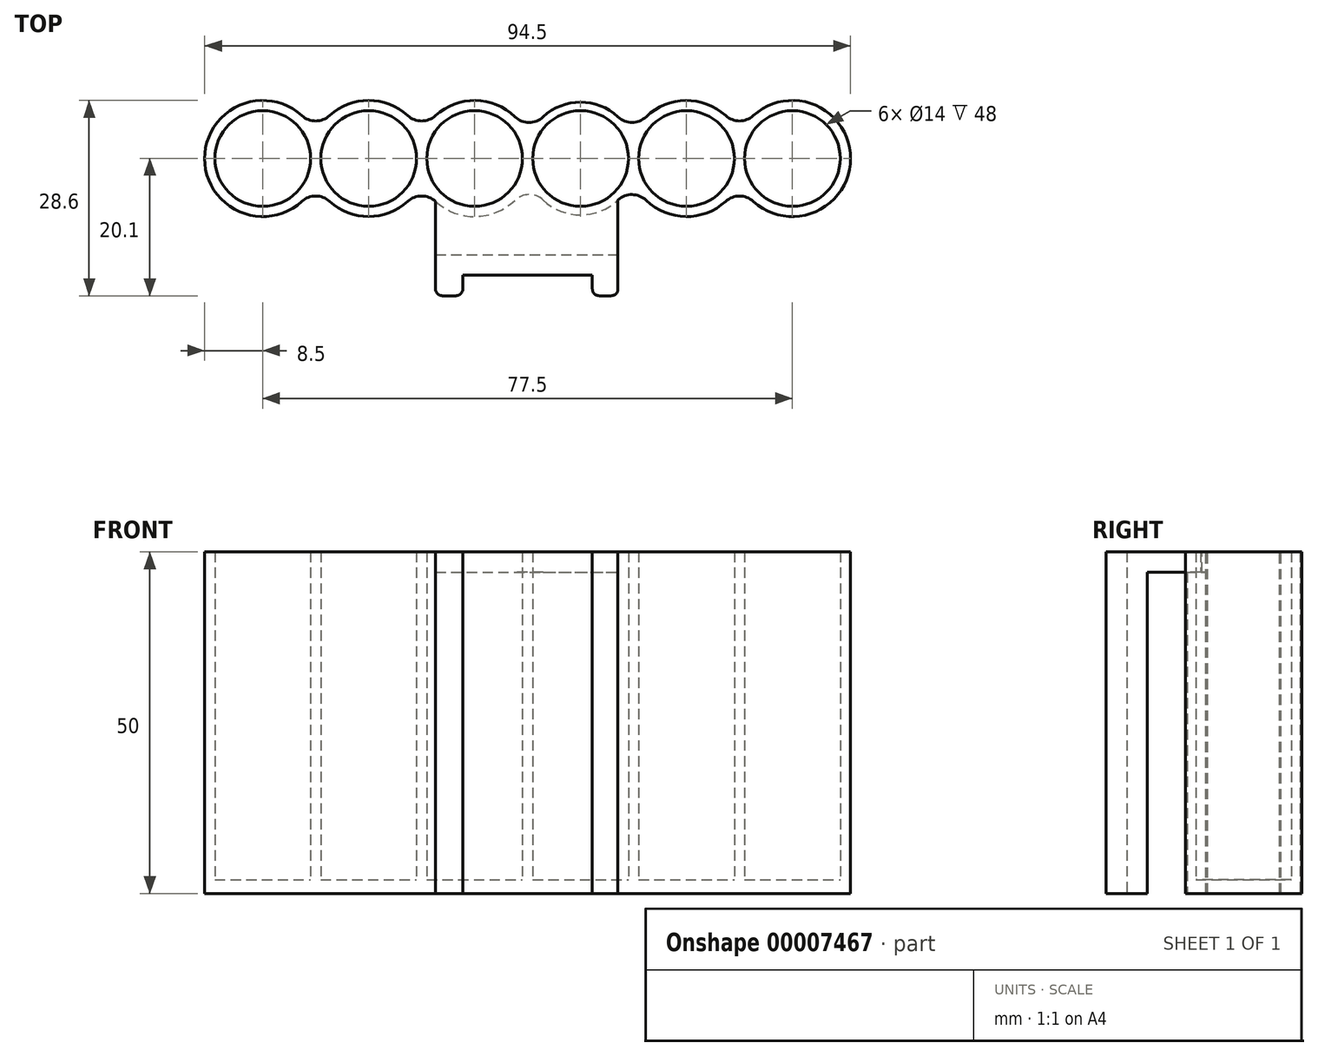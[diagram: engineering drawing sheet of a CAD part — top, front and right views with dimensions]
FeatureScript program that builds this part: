
annotation { "Feature Type Name" : "Feature", "Feature Type Description" : "" }
export const myFeature = defineFeature(function(context is Context, id is Id, definition is map)
    precondition{}
    {
        {
            var Q0;
            Q0=qCreatedBy(makeId("Top.planeOp"),FACE);
            var sketch = newSketch(context, id + "F0", { "sketchPlane" : qUnion([Q0])});
            skCircle(sketch, "E0", {"center": v(7.75, 0) * mm, "radius": 7 * mm});
            skCircle(sketch, "E1", {"center": v(23.25, 0) * mm, "radius": 7 * mm});
            skCircle(sketch, "E2", {"center": v(38.75, 0) * mm, "radius": 7 * mm});
            skCircle(sketch, "E3.0.MirrorC", {"center": v(-7.75, 0) * mm, "radius": 7 * mm});
            skCircle(sketch, "E4.0.MirrorC", {"center": v(-23.25, 0) * mm, "radius": 7 * mm});
            skCircle(sketch, "E5.0.MirrorC", {"center": v(-38.75, 0) * mm, "radius": 7 * mm});
            skArc(sketch, "E6", {"start": v(-31, 3.5) * mm, "mid": v(-47.25, 0) * mm, "end": v(-31, -3.5) * mm});
            skArc(sketch, "E7", {"start": v(-31, -3.5) * mm, "mid": v(-23.25, -8.5) * mm, "end": v(-15.5, -3.5) * mm});
            skArc(sketch, "E8", {"start": v(-15.5, -3.5) * mm, "mid": v(-7.46, -8.5) * mm, "end": v(0.22, -2.96) * mm});
            skArc(sketch, "E9", {"start": v(15.28, -2.96) * mm, "mid": v(22.96, -8.5) * mm, "end": v(31, -3.5) * mm});
            skArc(sketch, "E10", {"start": v(31, -3.5) * mm, "mid": v(47.25, 0) * mm, "end": v(31, 3.5) * mm});
            skArc(sketch, "E11.trimOffspring", {"start": v(-15.5, 3.5) * mm, "mid": v(-23.25, 8.5) * mm, "end": v(-31, 3.5) * mm});
            skArc(sketch, "E12.trimOffspring", {"start": v(0.22, 2.96) * mm, "mid": v(-7.46, 8.5) * mm, "end": v(-15.5, 3.5) * mm});
            skArc(sketch, "E13.trimOffspring", {"start": v(15.28, 2.96) * mm, "mid": v(7.75, 8.26) * mm, "end": v(0.22, 2.96) * mm});
            skArc(sketch, "E14.trimOffspring", {"start": v(31, 3.5) * mm, "mid": v(22.96, 8.5) * mm, "end": v(15.28, 2.96) * mm});
            skArc(sketch, "E15.trimOffspring", {"start": v(0.22, -2.96) * mm, "mid": v(7.75, -8.26) * mm, "end": v(15.28, -2.96) * mm});
            skSolve(sketch);
        }
        {
            var Q0;
            Q0 = qSketchRegion(id + "F0", true);
            extrude(context, id + "F1", {"entities" : qUnion([Q0]), "depth" : 50 * mm});
        }
        {
            var Q0;
            Q0=makeQuery(id+"F1.opExtrude","SWEPT_EDGE",EDGE,{"disambiguationData":[OSD([sQuery(id+"F0.wireOp",EDGE,"E6"),sQuery(id+"F0.wireOp",EDGE,"E11.trimOffspring")])]});
            var Q1;
            Q1=makeQuery(id+"F1.opExtrude","SWEPT_EDGE",EDGE,{"disambiguationData":[OSD([sQuery(id+"F0.wireOp",EDGE,"E11.trimOffspring"),sQuery(id+"F0.wireOp",EDGE,"E12.trimOffspring")])]});
            var Q2;
            Q2=makeQuery(id+"F1.opExtrude","SWEPT_EDGE",EDGE,{"disambiguationData":[OSD([sQuery(id+"F0.wireOp",EDGE,"E12.trimOffspring"),sQuery(id+"F0.wireOp",EDGE,"E13.trimOffspring")])]});
            var Q3;
            Q3=makeQuery(id+"F1.opExtrude","SWEPT_EDGE",EDGE,{"disambiguationData":[OSD([sQuery(id+"F0.wireOp",EDGE,"E13.trimOffspring"),sQuery(id+"F0.wireOp",EDGE,"E14.trimOffspring")])]});
            var Q4;
            Q4=makeQuery(id+"F1.opExtrude","SWEPT_EDGE",EDGE,{"disambiguationData":[OSD([sQuery(id+"F0.wireOp",EDGE,"E10"),sQuery(id+"F0.wireOp",EDGE,"E14.trimOffspring")])]});
            var Q5;
            Q5=makeQuery(id+"F1.opExtrude","SWEPT_EDGE",EDGE,{"disambiguationData":[OSD([sQuery(id+"F0.wireOp",EDGE,"E6"),sQuery(id+"F0.wireOp",EDGE,"E7")])]});
            var Q6;
            Q6=makeQuery(id+"F1.opExtrude","SWEPT_EDGE",EDGE,{"disambiguationData":[OSD([sQuery(id+"F0.wireOp",EDGE,"E7"),sQuery(id+"F0.wireOp",EDGE,"E8")])]});
            var Q7;
            Q7=makeQuery(id+"F1.opExtrude","SWEPT_EDGE",EDGE,{"disambiguationData":[OSD([sQuery(id+"F0.wireOp",EDGE,"E8"),sQuery(id+"F0.wireOp",EDGE,"1430ee90-bdf1-449c-a1c4-02042bd7a36f")])]});
            var Q8;
            Q8=makeQuery(id+"F1.opExtrude","SWEPT_EDGE",EDGE,{"disambiguationData":[OSD([sQuery(id+"F0.wireOp",EDGE,"1430ee90-bdf1-449c-a1c4-02042bd7a36f"),sQuery(id+"F0.wireOp",EDGE,"E9")])]});
            var Q9;
            Q9=makeQuery(id+"F1.opExtrude","SWEPT_EDGE",EDGE,{"disambiguationData":[OSD([sQuery(id+"F0.wireOp",EDGE,"E9"),sQuery(id+"F0.wireOp",EDGE,"E10")])]});
            fillet(context, id + "F2", {"entities" : qUnion([Q0, Q1, Q2, Q3, Q4, Q5, Q6, Q7, Q8, Q9]), "radius" : 3 * mm, "tangentPropagation" : true, "allowEdgeOverflow" : false});
        }
        {
            var Q0;
            Q0=makeQuery(id+"F1.opExtrude","CAP_FACE",FACE,{"disambiguationData":[OSD([sQuery(id+"F0.wireOp",EDGE,"E0"),sQuery(id+"F0.wireOp",EDGE,"E1"),sQuery(id+"F0.wireOp",EDGE,"E2"),sQuery(id+"F0.wireOp",EDGE,"E3.0.MirrorC"),sQuery(id+"F0.wireOp",EDGE,"E4.0.MirrorC"),sQuery(id+"F0.wireOp",EDGE,"E5.0.MirrorC"),sQuery(id+"F0.wireOp",EDGE,"E6"),sQuery(id+"F0.wireOp",EDGE,"E7"),sQuery(id+"F0.wireOp",EDGE,"E8"),sQuery(id+"F0.wireOp",EDGE,"1430ee90-bdf1-449c-a1c4-02042bd7a36f"),sQuery(id+"F0.wireOp",EDGE,"E9"),sQuery(id+"F0.wireOp",EDGE,"E10"),sQuery(id+"F0.wireOp",EDGE,"E11.trimOffspring"),sQuery(id+"F0.wireOp",EDGE,"E12.trimOffspring"),sQuery(id+"F0.wireOp",EDGE,"E13.trimOffspring"),sQuery(id+"F0.wireOp",EDGE,"E14.trimOffspring")])],"isStart":true});
            var sketch = newSketch(context, id + "F3", { "sketchPlane" : qUnion([Q0])});
            skArc(sketch, "E16.0", {"start": v(33.02, 6.28) * mm, "mid": v(47.25, 0) * mm, "end": v(33.02, -6.28) * mm});
            skArc(sketch, "E17.0", {"start": v(28.98, 6.28) * mm, "mid": v(31, 5.5) * mm, "end": v(33.02, 6.28) * mm});
            skArc(sketch, "E18.0", {"start": v(17.35, 6.12) * mm, "mid": v(23.14, 8.5) * mm, "end": v(28.98, 6.28) * mm});
            skArc(sketch, "E19.0", {"start": v(13.22, 6.1) * mm, "mid": v(15.3, 5.28) * mm, "end": v(17.35, 6.12) * mm});
            skArc(sketch, "E20.0", {"start": v(2.28, 6.1) * mm, "mid": v(7.75, 8.26) * mm, "end": v(13.22, 6.1) * mm});
            skArc(sketch, "E21.0", {"start": v(-1.85, 6.12) * mm, "mid": v(0.2, 5.28) * mm, "end": v(2.28, 6.1) * mm});
            skArc(sketch, "E22.0", {"start": v(-13.48, 6.28) * mm, "mid": v(-7.64, 8.5) * mm, "end": v(-1.85, 6.12) * mm});
            skArc(sketch, "E23.0", {"start": v(-17.52, 6.28) * mm, "mid": v(-15.5, 5.5) * mm, "end": v(-13.48, 6.28) * mm});
            skArc(sketch, "E24.0", {"start": v(-28.98, 6.28) * mm, "mid": v(-23.25, 8.5) * mm, "end": v(-17.52, 6.28) * mm});
            skArc(sketch, "E25.0", {"start": v(-33.02, 6.28) * mm, "mid": v(-31, 5.5) * mm, "end": v(-28.98, 6.28) * mm});
            skArc(sketch, "E26.0", {"start": v(-33.02, -6.28) * mm, "mid": v(-47.25, 0) * mm, "end": v(-33.02, 6.28) * mm});
            skArc(sketch, "E27.0", {"start": v(-28.98, -6.28) * mm, "mid": v(-31, -5.5) * mm, "end": v(-33.02, -6.28) * mm});
            skArc(sketch, "E28.0", {"start": v(-17.52, -6.28) * mm, "mid": v(-23.25, -8.5) * mm, "end": v(-28.98, -6.28) * mm});
            skArc(sketch, "E29.0", {"start": v(-13.48, -6.28) * mm, "mid": v(-15.5, -5.5) * mm, "end": v(-17.52, -6.28) * mm});
            skArc(sketch, "E30.0", {"start": v(-1.85, -6.12) * mm, "mid": v(-7.64, -8.5) * mm, "end": v(-13.48, -6.28) * mm});
            skArc(sketch, "E31.0", {"start": v(2.28, -6.1) * mm, "mid": v(0.2, -5.28) * mm, "end": v(-1.85, -6.12) * mm});
            skArc(sketch, "E32.0", {"start": v(13.22, -6.1) * mm, "mid": v(7.75, -8.26) * mm, "end": v(2.28, -6.1) * mm});
            skArc(sketch, "E33.0", {"start": v(17.35, -6.12) * mm, "mid": v(15.3, -5.28) * mm, "end": v(13.22, -6.1) * mm});
            skArc(sketch, "E34.0", {"start": v(28.98, -6.28) * mm, "mid": v(23.14, -8.5) * mm, "end": v(17.35, -6.12) * mm});
            skArc(sketch, "E35.0", {"start": v(33.02, -6.28) * mm, "mid": v(31, -5.5) * mm, "end": v(28.98, -6.28) * mm});
            skSolve(sketch);
        }
        {
            var Q0;
            Q0 = qSketchRegion(id + "F3", true);
            extrude(context, id + "F4", {"entities" : qUnion([Q0]), "operationType" : NewBodyOperationType.ADD, "oppositeDirection" : true, "depth" : 2 * mm});
        }
        {
            var Q0;
            Q0=makeQuery(id+"F1.opExtrude","CAP_FACE",FACE,{"disambiguationData":[OSD([sQuery(id+"F0.wireOp",EDGE,"E0"),sQuery(id+"F0.wireOp",EDGE,"E1"),sQuery(id+"F0.wireOp",EDGE,"E2"),sQuery(id+"F0.wireOp",EDGE,"E3.0.MirrorC"),sQuery(id+"F0.wireOp",EDGE,"E4.0.MirrorC"),sQuery(id+"F0.wireOp",EDGE,"E5.0.MirrorC"),sQuery(id+"F0.wireOp",EDGE,"E6"),sQuery(id+"F0.wireOp",EDGE,"E7"),sQuery(id+"F0.wireOp",EDGE,"E8"),sQuery(id+"F0.wireOp",EDGE,"1430ee90-bdf1-449c-a1c4-02042bd7a36f"),sQuery(id+"F0.wireOp",EDGE,"E9"),sQuery(id+"F0.wireOp",EDGE,"E10"),sQuery(id+"F0.wireOp",EDGE,"E11.trimOffspring"),sQuery(id+"F0.wireOp",EDGE,"E12.trimOffspring"),sQuery(id+"F0.wireOp",EDGE,"E13.trimOffspring"),sQuery(id+"F0.wireOp",EDGE,"E14.trimOffspring")])],"isStart":false});
            var sketch = newSketch(context, id + "F5", { "sketchPlane" : qUnion([Q0])});
            skArc(sketch, "E36.0", {"start": v(-13.48, -6.28) * mm, "mid": v(-2.02, 6.28) * mm, "end": v(-13.48, -6.28) * mm});
            skLineSegment(sketch, "E37", {"start": v(-13.48, -6.28) * mm, "end": v(-13.48, -14.1) * mm});
            skLineSegment(sketch, "E38", {"start": v(-13.48, -14.1) * mm, "end": v(13.22, -14.1) * mm});
            skLineSegment(sketch, "E39", {"start": v(13.22, -14.1) * mm, "end": v(13.22, -6.1) * mm});
            skArc(sketch, "E40.0", {"start": v(-13.48, -6.28) * mm, "mid": v(-7.64, -8.5) * mm, "end": v(-1.85, -6.12) * mm});
            skArc(sketch, "E41.0", {"start": v(-1.85, -6.12) * mm, "mid": v(0.2, -5.28) * mm, "end": v(2.28, -6.1) * mm});
            skArc(sketch, "E42.0", {"start": v(2.28, -6.1) * mm, "mid": v(7.75, -8.26) * mm, "end": v(13.22, -6.1) * mm});
            skSolve(sketch);
        }
        {
            var Q0;
            Q0 = qSketchRegion(id + "F5", true);
            extrude(context, id + "F6", {"entities" : qUnion([Q0]), "operationType" : NewBodyOperationType.ADD, "oppositeDirection" : true, "depth" : 3 * mm});
        }
        {
            var Q0;
            Q0=makeQuery(id+"F6.opExtrude","SWEPT_FACE",FACE,{"disambiguationData":[OSD([sQuery(id+"F5.wireOp",EDGE,"E38")])]});
            var sketch = newSketch(context, id + "F7", { "sketchPlane" : qUnion([Q0])});
            skLineSegment(sketch, "E43.0", {"start": v(-13.48, 50) * mm, "end": v(13.22, 50) * mm});
            skLineSegment(sketch, "E44.0", {"start": v(-13.48, 0) * mm, "end": v(-13.48, 0) * mm});
            skLineSegment(sketch, "E45.0", {"start": v(-13.48, 0) * mm, "end": v(2.08, 0) * mm});
            skLineSegment(sketch, "E46.0", {"start": v(2.08, 0) * mm, "end": v(13.22, 0) * mm});
            skLineSegment(sketch, "E47", {"start": v(-13.48, 50) * mm, "end": v(-13.48, 0) * mm});
            skLineSegment(sketch, "E48", {"start": v(13.22, 50) * mm, "end": v(13.22, 0) * mm});
            skSolve(sketch);
        }
        {
            var Q0;
            Q0 = qSketchRegion(id + "F7", true);
            extrude(context, id + "F8", {"entities" : qUnion([Q0]), "operationType" : NewBodyOperationType.ADD, "depth" : 3 * mm});
        }
        {
            var Q0;
            Q0=makeQuery(id+"F8.opExtrude","CAP_FACE",FACE,{"disambiguationData":[OSD([sQuery(id+"F7.wireOp",EDGE,"E43.0"),sQuery(id+"F7.wireOp",EDGE,"E44.0"),sQuery(id+"F7.wireOp",EDGE,"E45.0"),sQuery(id+"F7.wireOp",EDGE,"E46.0"),sQuery(id+"F7.wireOp",EDGE,"E47"),sQuery(id+"F7.wireOp",EDGE,"E48")])],"isStart":false});
            var sketch = newSketch(context, id + "F9", { "sketchPlane" : qUnion([Q0])});
            skLineSegment(sketch, "E49.0", {"start": v(-13.48, 50) * mm, "end": v(-13.48, 50) * mm});
            skLineSegment(sketch, "E50.0", {"start": v(13.22, 0) * mm, "end": v(13.22, 50) * mm});
            skLineSegment(sketch, "E51", {"start": v(-9.48, 50) * mm, "end": v(-9.48, 0) * mm});
            skLineSegment(sketch, "E52.0.MirrorCS", {"start": v(9.48, 50) * mm, "end": v(9.48, 0) * mm});
            skLineSegment(sketch, "E53.0", {"start": v(-13.48, 0) * mm, "end": v(-13.48, 50) * mm});
            skLineSegment(sketch, "E54", {"start": v(-13.48, 50) * mm, "end": v(-9.48, 50) * mm});
            skLineSegment(sketch, "E55", {"start": v(9.48, 50) * mm, "end": v(13.22, 50) * mm});
            skLineSegment(sketch, "E56", {"start": v(13.22, 0) * mm, "end": v(9.48, 0) * mm});
            skLineSegment(sketch, "E57", {"start": v(-9.48, 0) * mm, "end": v(-13.48, 0) * mm});
            skSolve(sketch);
        }
        {
            var Q0;
            Q0 = qSketchRegion(id + "F9", true);
            extrude(context, id + "F10", {"entities" : qUnion([Q0]), "operationType" : NewBodyOperationType.ADD, "depth" : 3 * mm});
        }
        {
            var Q0;
            Q0=makeQuery(id+"F10.opExtrude","CAP_EDGE",EDGE,{"disambiguationData":[OSD([sQuery(id+"F9.wireOp",EDGE,"E49.0")])],"isStart":false});
            var Q1;
            Q1=makeQuery(id+"F10.opExtrude","CAP_EDGE",EDGE,{"disambiguationData":[OSD([sQuery(id+"F9.wireOp",EDGE,"E51")])],"isStart":false});
            var Q2;
            Q2=makeQuery(id+"F10.opExtrude","CAP_EDGE",EDGE,{"disambiguationData":[OSD([sQuery(id+"F9.wireOp",EDGE,"E52.0.MirrorCS")])],"isStart":false});
            var Q3;
            Q3=makeQuery(id+"F10.opExtrude","CAP_EDGE",EDGE,{"disambiguationData":[OSD([sQuery(id+"F9.wireOp",EDGE,"E50.0")])],"isStart":false});
            var Q4;
            Q4=makeQuery(id+"F10.opExtrude","CAP_EDGE",EDGE,{"disambiguationData":[OSD([sQuery(id+"F9.wireOp",EDGE,"E53.0")])],"isStart":false});
            fillet(context, id + "F11", {"entities" : qUnion([Q0, Q1, Q2, Q3, Q4]), "radius" : 1 * mm, "tangentPropagation" : true, "allowEdgeOverflow" : false});
        }
    });
